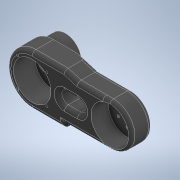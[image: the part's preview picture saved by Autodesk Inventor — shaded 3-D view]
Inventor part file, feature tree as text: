
AUTODESK INVENTOR PART (.ipt)
format: ipt  version: 2021 (Build 250183000, 183)  size: 497,152 bytes
history: native  units: mm
features: sketch x13, extrude x10, hole x3, fillet x3, pattern_circular x1
ambient origin geometry x8: Origin, YZ Plane, XZ Plane, XY Plane, X Axis, Y Axis, Z Axis, Center Point
bodies: Body1 (feature_tree)
feature tree (30):
  sketch  "Boceto1"  dims[d1=66.0mm d30=78.0mm]
  extrude  "Extrusión4"  Depth=78.0mm
  extrude  "Extrusión5"  Depth=6.0mm TaperAngle=0.0deg
  hole  "Agujero2"  [1 undecoded]
  pattern_circular  "Patrón circular2"  Count=6 Angle=360.0deg
  sketch  "Boceto4"  dims[d72=40.0mm d73=16.0mm]
  fillet  "Empalme5"  Radius=50.0mm
  fillet  "Empalme6"  Radius=50.0mm
  sketch  "Boceto6"  dims[d74=3.0mm]
  sketch  "Boceto7"  dims[d75=3.688101mm d76=9.0mm d77=4.0mm d78=2.0mm d79=90.0deg d80=13.0mm d81=0.0mm d82=60.0mm d83=360.0deg]
  sketch  "Boceto10"  dims[d85=50.0mm d86=32.0mm d87=12.0mm d88=11.65mm d89=10.5mm d90=7.0mm d91=21.0mm d92=2.8mm d93=4.4mm d94=5.6mm d95=4.4mm d96=0.8mm d97=0.8mm d98=0.8mm d99=0.8mm d100=0.8mm d101=0.8mm d102=2.0mm d103=2.0mm d104=2.0mm d105=2.0mm d106=2.0mm d107=2.0mm d108=2.0mm d109=2.0mm d110=2.0mm d111=2.0mm d136=50.0mm d137=50.0mm]
  extrude  "Extrusión15"  Depth=20.0mm
  sketch  "Boceto12"  dims[d188=50.0mm d189=50.0mm]
  extrude  "Extrusión16"  Depth=50.0mm
  extrude  "Extrusión17"  Depth=10.0mm
  sketch  "Boceto14"  dims[d191=6.0mm d192=10.0mm]
  extrude  "Extrusión19"  Depth=10.0mm
  extrude  "Extrusión20"  Depth=70.0mm
  hole  "Agujero7"  [1 undecoded]
  extrude  "Extrusión21"  Depth=2.0mm TaperAngle=360.0deg
  hole  "Agujero8"  [1 undecoded]
  extrude  "Extrusión22"  Depth=2.0mm TaperAngle=360.0deg
  extrude  "Extrusión23"  Depth=2.0mm
  fillet  "Empalme7"  Radius=3.0mm
  sketch  "Boceto3"  dims[d38=33.0mm d39=0.0mm d40=6.0mm d41=0.0mm]
  sketch  "Boceto11"  dims[d149=6.0mm d187=20.0mm]
  sketch  "Boceto15"  dims[d193=10.0mm d194=33.0mm]
  sketch  "Boceto16"  dims[d195=19.999999mm d196=70.0mm]
  sketch  "Boceto17"  dims[d197=32.0mm d198=45.0deg]
  sketch  "Boceto18"  dims[d199=3.0mm d200=40.0mm d202=360.0deg d213=60.0mm d280=40.0mm d282=360.0deg d284=60.0mm d285=3.0mm d286=0.0mm d287=32.0mm d288=50.0mm d289=23.0mm d290=11.5mm d291=2.2mm d292=2.2mm d293=2.2mm d294=2.2mm d295=2.2mm d296=2.2mm d297=2.2mm d298=2.2mm d299=2.2mm d300=2.2mm d301=27.0mm d302=16.0mm d303=8.0mm d304=13.5mm d305=13.5mm d306=8.0mm d307=8.0mm d308=8.0mm d309=8.0mm d310=8.0mm d311=8.0mm d312=6.0mm d313=8.307mm d314=22.006mm d315=1.042mm d316=1.042mm d317=11.2mm d318=0.8mm d319=0.8mm d320=0.8mm d321=0.8mm d322=1.75mm d323=0.8mm d324=1.75mm d325=0.8mm d360=3.0mm d361=0.0mm d362=2.4mm d363=0.0mm d367=49.235mm d368=3.0mm d369=0.0mm d370=28.934mm d371=0.0mm d372=58.0mm d373=32.0mm d374=135.0deg d375=3.0mm d376=40.0mm d378=360.0deg d380=3.688101mm d381=9.0mm d382=4.0mm d383=2.0mm d384=90.0deg d385=13.0mm d386=0.0mm d387=120.0mm d388=13.736mm d389=22.934mm d390=0.0mm d391=2.112861mm d392=5.2mm d393=4.0mm d394=2.0mm d395=90.0deg d396=7.8mm d397=20.594885mm d398=6.0mm d399=0.0mm d400=64.0mm d401=3.0mm d402=0.0mm d403=2.0mm d53=0.5mm d54=0.872665mm d55=0.5mm d56=0.872665mm]
note: 3 required parameter values undecoded (feature->parameter linkage not recoverable at this tier; creation-order binding heuristic only, values carry confidence <= 0.55)
